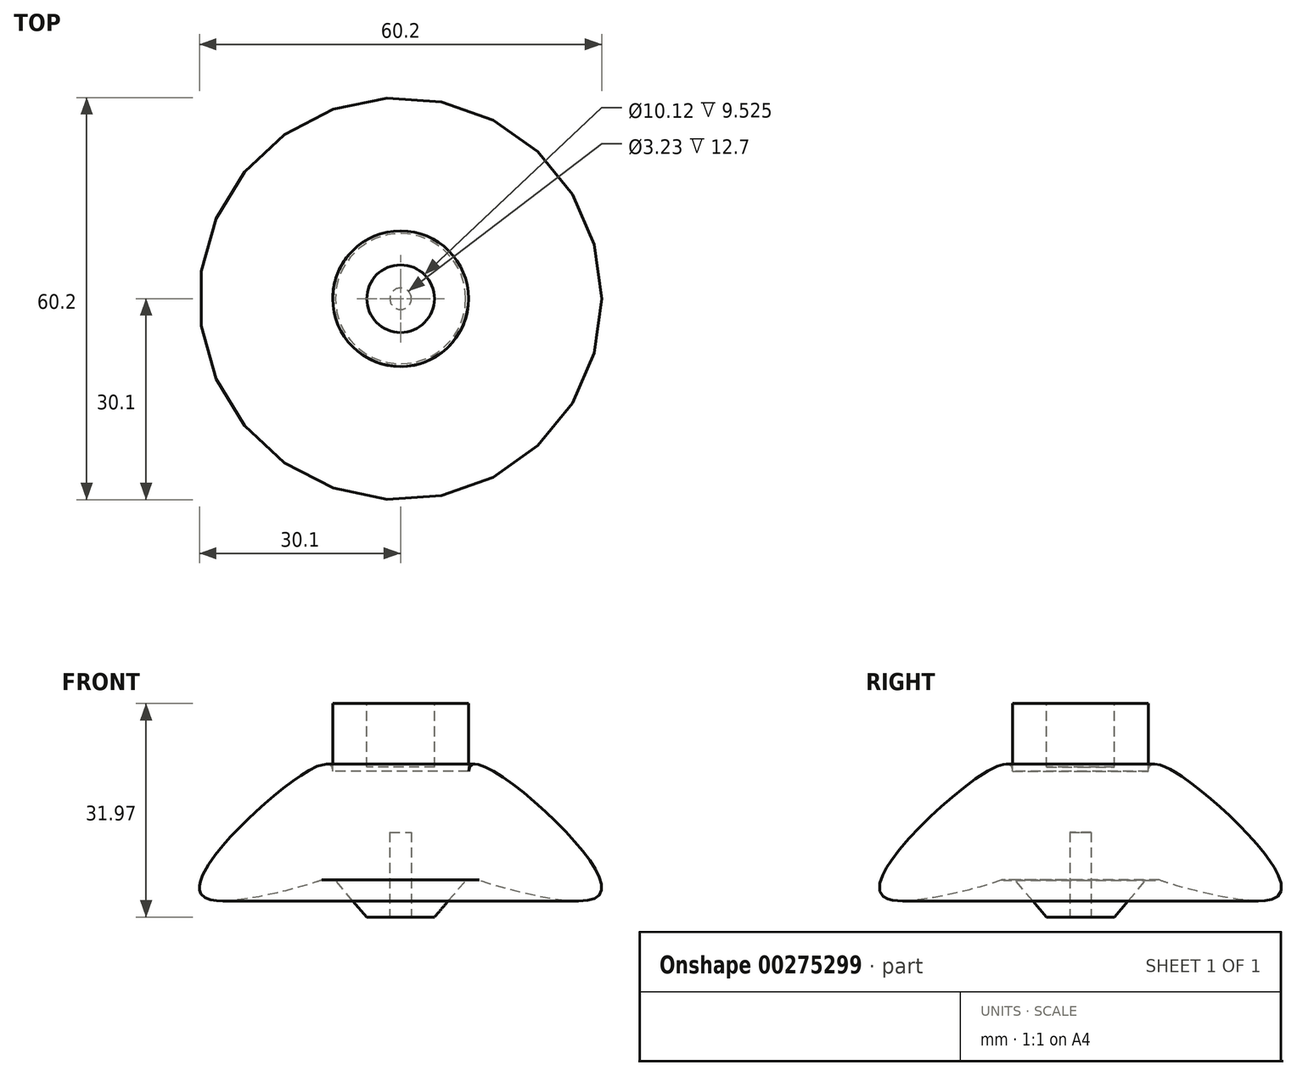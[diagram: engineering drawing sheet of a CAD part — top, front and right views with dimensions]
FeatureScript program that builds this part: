
annotation { "Feature Type Name" : "Feature", "Feature Type Description" : "" }
export const myFeature = defineFeature(function(context is Context, id is Id, definition is map)
    precondition{}
    {
        {
            var Q0;
            Q0=qCreatedBy(makeId("Front.planeOp"),FACE);
            var sketch = newSketch(context, id + "F0", { "sketchPlane" : qUnion([Q0])});
            skLineSegment(sketch, "E0", {"start": v(5.08, 0) * mm, "end": v(0, 0) * mm});
            skLineSegment(sketch, "E1", {"start": v(9.75, 5.47) * mm, "end": v(5.08, 0) * mm});
            skFitSpline(sketch, "E2", {"points": [v(9.75, 5.47) * mm, v(11.99, 5.47) * mm, v(29.09, 2.8) * mm, v(22.4, 15.09) * mm, v(10.16, 21.81) * mm], "startDerivative": vector(70.73, 0) * mm, "endDerivative": vector(0, -34.8) * mm});
            skLineSegment(sketch, "E3", {"start": v(10.16, 21.81) * mm, "end": v(10.16, 25.11) * mm});
            skLineSegment(sketch, "E4", {"start": v(10.16, 21.81) * mm, "end": v(10.16, 31.97) * mm});
            skLineSegment(sketch, "E5", {"start": v(10.16, 31.97) * mm, "end": v(0, 31.97) * mm});
            skLineSegment(sketch, "E6", {"start": v(0, 31.97) * mm, "end": v(0, 0) * mm});
            skPoint(sketch, "E7", {"position": v(16.99, 4) * mm});
            skPoint(sketch, "E8", {"position": v(29.47, 6.57) * mm});
            skSolve(sketch);
        }
        {
            var Q0;
            Q0=makeQuery(id+"F0.imprint","IMPRINT",FACE,{"disambiguationData":[TD([[makeQuery(id+"F0.imprint","IMPRINT",EDGE,{"derivedFrom":sQuery(id+"F0.wireOp",EDGE,"E0")}),-1.0]])]});
            var Q1;
            Q1=sQuery(id+"F0.wireOp",EDGE,"E6");
            revolve(context, id + "F1", {"entities" : qUnion([Q0]), "axis" : qUnion([Q1]), "revolveType" : RevolveType.FULL});
        }
        {
            var Q0;
            Q0=makeQuery(id+"F1.opRevolve","SWEPT_FACE",FACE,{"disambiguationData":[OSD([sQuery(id+"F0.wireOp",EDGE,"E5")])]});
            var sketch = newSketch(context, id + "F2", { "sketchPlane" : qUnion([Q0])});
            skCircle(sketch, "E9", {"center": v(0, 0) * mm, "radius": 5.06 * mm});
            skSolve(sketch);
        }
        {
            var Q0;
            Q0 = qSketchRegion(id + "F2", true);
            extrude(context, id + "F3", {"entities" : qUnion([Q0]), "operationType" : NewBodyOperationType.REMOVE, "oppositeDirection" : true, "depth" : 9.52 * mm});
        }
        {
            var Q0;
            Q0=makeQuery(id+"F1.opRevolve","SWEPT_FACE",FACE,{"disambiguationData":[OSD([sQuery(id+"F0.wireOp",EDGE,"E0")])]});
            var sketch = newSketch(context, id + "F4", { "sketchPlane" : qUnion([Q0])});
            skCircle(sketch, "E10", {"center": v(0, 0) * mm, "radius": 1.61 * mm});
            skSolve(sketch);
        }
        {
            var Q0;
            Q0=makeQuery(id+"F4.imprint","IMPRINT",FACE,{"disambiguationData":[TD([[makeQuery(id+"F4.imprint","IMPRINT",EDGE,{"derivedFrom":sQuery(id+"F4.wireOp",EDGE,"E10")}),1.0]])]});
            var Q1;
            Q1=sQuery(id+"F4.wireOp",EDGE,"E10");
            extrude(context, id + "F5", {"entities" : qUnion([Q0]), "operationType" : NewBodyOperationType.REMOVE, "surfaceEntities" : qUnion([Q1]), "oppositeDirection" : true, "depth" : 12.7 * mm});
        }
    });
